# Revit family: Plumbing Fixture-FloorDrain_Mifab_C1400-RD
name_source: partatom
category: Plumbing Fixtures
revit_build: Autodesk Revit Structure 2013 (Build: 20120221_2030(x64)
units: mm (PartAtom-declared; Revit-internal decimal feet)

## types (6) — shared parameters
Body Height = 3.5 "
Floor Drain Material = Paint - Sherwin Williams Paint - #952C2A - Bellwood Red
Manufacturer = MIFAB
Model = C1400-RD
URL = WWW.MIFAB.COM
zero-valued in all types: Default Elevation, WFU

## per-type parameters (varying)
| type | Description | Stainer Diameter | Stainer Radius |
| 3" | STAINLESS STEEL ROUND, SMOOTH, WALL ACCESS COVER WITH SCREW | 3 " | 1.5 " |
| 4" | STAINLESS STEEL ROUND, SMOOTH, WALL ACCESS COVER WITH SCREW | 4 " | 2 " |
| 6" | STAINLESS STEEL ROUND, SMOOTH,WALL ACCESS COVER WITH SCREW | 6 " | 3 " |
| 8" | STAINLESS STEEL ROUND, SMOOTH, WALL ACCESS COVER WITH SCREW | 8 " | 4 " |
| 5" | STAINLESS STEEL ROUND, SMOOTH, WALL ACCESS COVER WITH SCREW | 5 " | 2.5 " |
| 10" | STAINLESS STEEL ROUND, SMOOTH, WALL ACCESS COVER WITH SCREW | 10 " | 5 " |

## geometry (parser evidence)
native form markers: Blend x3, Sweep x1
no freeform markers — native parametric forms only
